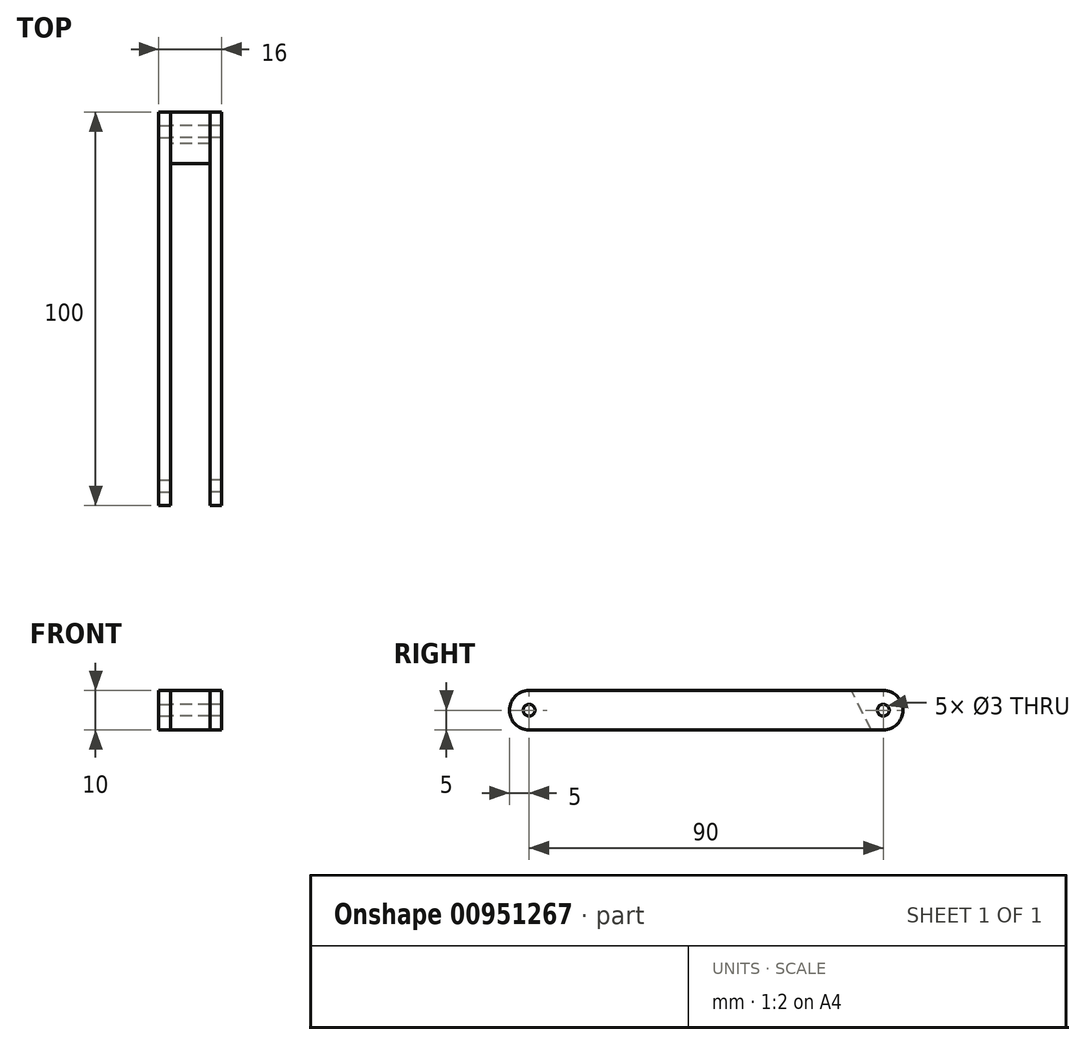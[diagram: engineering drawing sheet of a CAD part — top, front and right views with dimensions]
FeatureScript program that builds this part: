
annotation { "Feature Type Name" : "Feature", "Feature Type Description" : "" }
export const myFeature = defineFeature(function(context is Context, id is Id, definition is map)
    precondition{}
    {
        {
            var Q0;
            Q0=qCreatedBy(makeId("Right.planeOp"),FACE);
            cPlane(context, id + "F0", {"entities" : qUnion([Q0]), "cplaneType" : CPlaneType.OFFSET, "offset" : 5 * mm, "width" : 150 * mm, "height" : 150 * mm});
        }
        {
            var Q0;
            Q0=qCreatedBy(id+"F0.planeOp",FACE);
            var sketch = newSketch(context, id + "F1", { "sketchPlane" : qUnion([Q0])});
            skLineSegment(sketch, "E0.bottom", {"start": v(-45, 5) * mm, "end": v(45, 5) * mm});
            skLineSegment(sketch, "E0.top", {"start": v(-45, -5) * mm, "end": v(45, -5) * mm});
            skLineSegment(sketch, "E0.left", {"start": v(-50, 0) * mm, "end": v(-50, 0) * mm});
            skLineSegment(sketch, "E0.right", {"start": v(50, 0) * mm, "end": v(50, 0) * mm});
            skPoint(sketch, "E0.middle", {"position": v(0, 0) * mm});
            skPoint(sketch, "E1.visualSharp", {"position": v(-50, -5) * mm});
            skArc(sketch, "E1.filletArc", {"start": v(-50, 0) * mm, "mid": v(-48.54, -3.54) * mm, "end": v(-45, -5) * mm});
            skPoint(sketch, "E2.visualSharp", {"position": v(50, 5) * mm});
            skArc(sketch, "E2.filletArc", {"start": v(50, 0) * mm, "mid": v(48.54, 3.54) * mm, "end": v(45, 5) * mm});
            skPoint(sketch, "E3.visualSharp", {"position": v(50, -5) * mm});
            skArc(sketch, "E3.filletArc", {"start": v(45, -5) * mm, "mid": v(48.54, -3.54) * mm, "end": v(50, 0) * mm});
            skPoint(sketch, "E4.visualSharp", {"position": v(-50, 5) * mm});
            skArc(sketch, "E4.filletArc", {"start": v(-45, 5) * mm, "mid": v(-48.54, 3.54) * mm, "end": v(-50, 0) * mm});
            skCircle(sketch, "E5", {"center": v(-45, 0) * mm, "radius": 1.5 * mm});
            skCircle(sketch, "E6", {"center": v(45, 0) * mm, "radius": 1.5 * mm});
            skSolve(sketch);
        }
        {
            var Q0;
            Q0=makeQuery(id+"F1.imprint","IMPRINT",FACE,{"disambiguationData":[TD([[makeQuery(id+"F1.imprint","IMPRINT",EDGE,{"derivedFrom":sQuery(id+"F1.wireOp",EDGE,"E0.bottom")}),-1.0]])]});
            extrude(context, id + "F2", {"entities" : qUnion([Q0]), "depth" : 3 * mm, "offsetDistance" : 25 * mm});
        }
        {
            var Q0;
            Q0=qCreatedBy(makeId("Right.planeOp"),FACE);
            cPlane(context, id + "F3", {"entities" : qUnion([Q0]), "cplaneType" : CPlaneType.OFFSET, "offset" : 5 * mm, "oppositeDirection" : true, "width" : 150 * mm, "height" : 150 * mm});
        }
        {
            var Q0;
            Q0=qCreatedBy(id+"F3.planeOp",FACE);
            var sketch = newSketch(context, id + "F4", { "sketchPlane" : qUnion([Q0])});
            skArc(sketch, "E7.0.0", {"start": v(-45, -5) * mm, "mid": v(-50, 0) * mm, "end": v(-45, 5) * mm});
            skLineSegment(sketch, "E7.0.1", {"start": v(-45, 5) * mm, "end": v(45, 5) * mm});
            skArc(sketch, "E7.0.2", {"start": v(45, 5) * mm, "mid": v(50, 0) * mm, "end": v(45, -5) * mm});
            skLineSegment(sketch, "E7.0.3", {"start": v(45, -5) * mm, "end": v(-45, -5) * mm});
            skCircle(sketch, "E8.0", {"center": v(45, 0) * mm, "radius": 1.5 * mm});
            skCircle(sketch, "E9.0", {"center": v(-45, 0) * mm, "radius": 1.5 * mm});
            skSolve(sketch);
        }
        {
            var Q0;
            Q0=makeQuery(id+"F4.imprint","IMPRINT",FACE,{"disambiguationData":[TD([[makeQuery(id+"F4.imprint","IMPRINT",EDGE,{"derivedFrom":sQuery(id+"F4.wireOp",EDGE,"E8.0")}),-1.0]])]});
            extrude(context, id + "F5", {"entities" : qUnion([Q0]), "oppositeDirection" : true, "depth" : 3 * mm, "offsetDistance" : 25 * mm});
        }
        {
            var Q0;
            Q0=makeQuery(id+"F5.opExtrude","CAP_FACE",FACE,{"disambiguationData":[OSD([sQuery(id+"F4.wireOp",EDGE,"E8.0"),sQuery(id+"F4.wireOp",EDGE,"E7.0.0"),sQuery(id+"F4.wireOp",EDGE,"E7.0.1"),sQuery(id+"F4.wireOp",EDGE,"E7.0.2"),sQuery(id+"F4.wireOp",EDGE,"E7.0.3"),sQuery(id+"F4.wireOp",EDGE,"E9.0")])],"isStart":true});
            var sketch = newSketch(context, id + "F6", { "sketchPlane" : qUnion([Q0])});
            skLineSegment(sketch, "E10", {"start": v(49.71, -9.33) * mm, "end": v(40.29, 9.33) * mm, "construction": true});
            skArc(sketch, "E11.0.startCap", {"start": v(54.18, -7.08) * mm, "mid": v(51.97, -13.8) * mm, "end": v(45.25, -11.58) * mm});
            skArc(sketch, "E11.0.endCap", {"start": v(35.82, 7.08) * mm, "mid": v(38.03, 13.8) * mm, "end": v(44.75, 11.58) * mm});
            skLineSegment(sketch, "E11.0.left", {"start": v(45.25, -11.58) * mm, "end": v(35.82, 7.08) * mm});
            skLineSegment(sketch, "E12.0.right", {"start": v(54.18, -7.08) * mm, "end": v(53.13, -5) * mm});
            skLineSegment(sketch, "E13", {"start": v(45, 0) * mm, "end": v(145, 0) * mm, "construction": true});
            skPoint(sketch, "E13.endSnap0", {"position": v(45, 0) * mm});
            skLineSegment(sketch, "E14.bottom", {"start": v(48.08, 5) * mm, "end": v(140, 5) * mm});
            skLineSegment(sketch, "E14.right", {"start": v(145, 0) * mm, "end": v(145, 0) * mm});
            skPoint(sketch, "E14.middle", {"position": v(95, 0) * mm});
            skPoint(sketch, "E15.visualSharp", {"position": v(145, -5) * mm});
            skArc(sketch, "E15.filletArc", {"start": v(140, -5) * mm, "mid": v(143.54, -3.54) * mm, "end": v(145, 0) * mm});
            skPoint(sketch, "E16.visualSharp", {"position": v(145, 5) * mm});
            skArc(sketch, "E16.filletArc", {"start": v(145, 0) * mm, "mid": v(143.54, 3.54) * mm, "end": v(140, 5) * mm});
            skLineSegment(sketch, "E17.trimOffspring", {"start": v(53.13, -5) * mm, "end": v(140, -5) * mm});
            skPoint(sketch, "E18.orphan", {"position": v(45, -5) * mm});
            skLineSegment(sketch, "E19.trimOffspring", {"start": v(48.08, 5) * mm, "end": v(44.75, 11.58) * mm});
            skPoint(sketch, "E20.orphan", {"position": v(45, 5) * mm});
            skCircle(sketch, "E21", {"center": v(40.29, 9.33) * mm, "radius": 1.5 * mm});
            skCircle(sketch, "E22", {"center": v(49.71, -9.33) * mm, "radius": 1.5 * mm});
            skSolve(sketch);
        }
        {
            var Q0;
            Q0=makeQuery(id+"F6.imprint","IMPRINT",FACE,{"disambiguationData":[TD([[makeQuery(id+"F6.imprint","IMPRINT",EDGE,{"derivedFrom":makeQuery(id+"F5.opExtrude","CAP_EDGE",EDGE,{"disambiguationData":[OSD([sQuery(id+"F4.wireOp",EDGE,"E8.0")])],"isStart":true})}),-1.0]])]});
            var Q1;
            {var subQ0=sQuery(id+"F6.wireOp",EDGE,"E11.0.startCap");Q1=makeQuery(id+"F6.imprint","IMPRINT",FACE,{"disambiguationData":[TD([[makeQuery(id+"F6.imprint","IMPRINT",EDGE,{"derivedFrom":subQ0}),-1.0]])]});}
            extrude(context, id + "F7", {"entities" : qUnion([Q0, Q1]), "depth" : 10 * mm, "offsetDistance" : 25 * mm});
        }
    });
